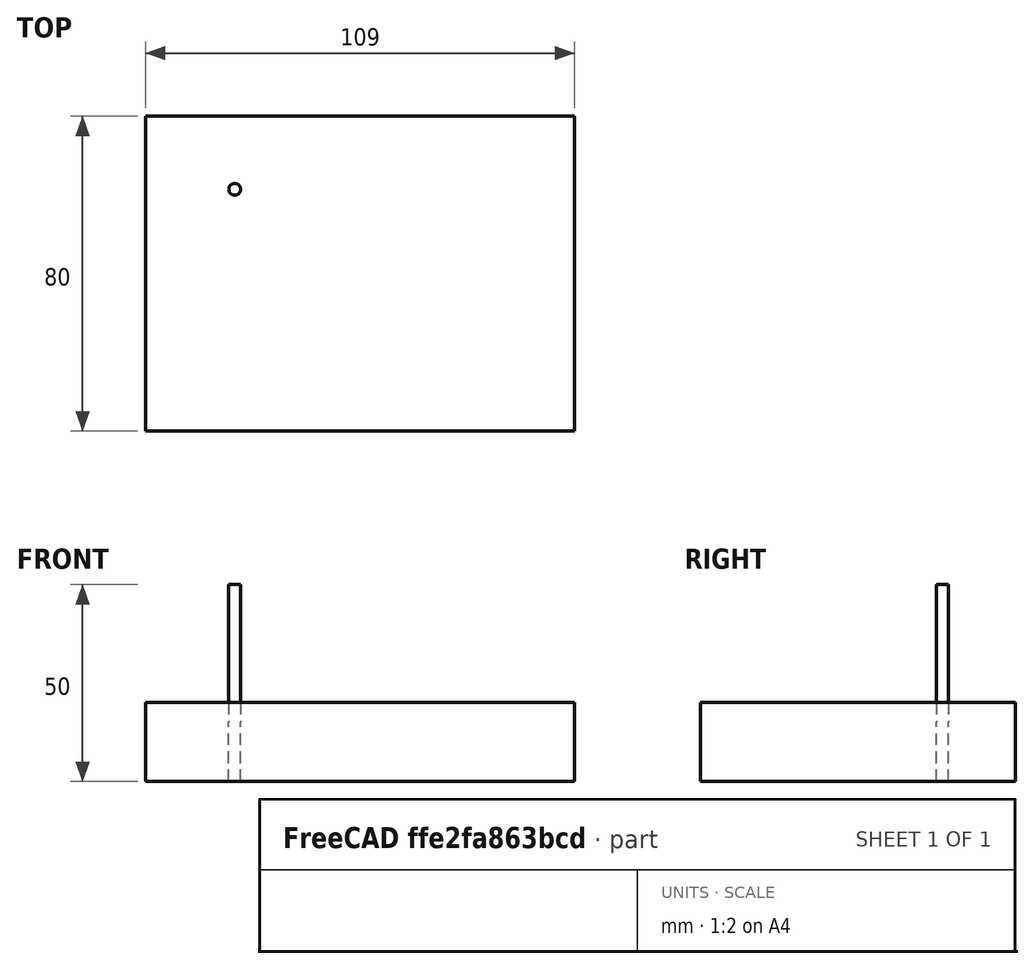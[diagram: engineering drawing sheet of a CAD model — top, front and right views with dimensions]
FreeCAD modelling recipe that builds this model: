
FCSTD DOCUMENT  (FreeCAD 0.21R33668 +26 (Git))
Label: Profile_20_80V_3mm
License: All rights reserved
LicenseURL: https://en.wikipedia.org/wiki/All_rights_reserved
objects: Path::FeaturePython×5, Sketcher::SketchObject×4, PartDesign::Pocket×3, Part::FeaturePython×3, App::DocumentObjectGroup×3, Mesh::FeaturePython×2, PartDesign::Pad×1, Spreadsheet::Sheet×1, App::FeaturePython×1, PartDesign::Fillet×1, PartDesign::Body×1
note: 21 computed .brp shape members not serialized (recipe doc carries the construction recipe); baked Part::Feature solids carry a one-line shape summary decoded from their .brp

FEATURE [Sketcher::SketchObject] Sketch  label="Sketch_Profile"
  FullyConstrained = true
  MapMode = 5
  Placement = pos=(0,0,0) rot=(1,0,0;1.5708rad)
  Support = -> [XZ_Plane]
  expr: Constraints[3] = Spreadsheet.Width
  expr: Constraints[4] = Spreadsheet.Height
  sketch-geometry (4):
    g0: LineSegment StartX=40 StartY=0 StartZ=0 EndX=40 EndY=-20 EndZ=0
    g1: LineSegment StartX=40 StartY=-20 StartZ=0 EndX=-40 EndY=-20 EndZ=0
    g2: LineSegment StartX=-40 StartY=-20 StartZ=0 EndX=-40 EndY=0 EndZ=0
    g3: LineSegment StartX=-40 StartY=0 StartZ=0 EndX=40 EndY=0 EndZ=0
  constraints (11):
    c: Horizontal(g1)
    c: Vertical(g0)
    c: Vertical(g2)
    c: DistanceX(g2,g0) = 80
    c: DistanceY(g2,g2) = 20
    c: Symmetric(g2,g0,g-1)
    c: Coincident(g3,g2)
    c: Horizontal(g3)
    c: Coincident(g0,g1)
    c: Coincident(g1,g2)
    c: Coincident(g3,g0)
FEATURE [PartDesign::Pad] Pad  label="Profile"
  Direction = (0,-1,-2e-16)
  Length = 105
  Length2 = 10
  Midplane = true
  Placement = pos=(0,0,0) rot=(1,0,0;1.5708rad)
  Profile = -> Sketch
  ReferenceAxis = -> Sketch [N_Axis]
  Type = 0
FEATURE [Spreadsheet::Sheet] Spreadsheet
  cells = A3='Height; B3(Height)=20; A4='Width; B4(Width)=80; A5='Slot_Height; B5(Slot_Height)=5.54; A7='V_Slot; B7(V_Slot)=20
FEATURE [App::FeaturePython] SetupSheet  # Path/CAM operation (typed FeaturePython)
  ClearanceHeightExpression = OpStockZMax+SetupSheet.ClearanceHeightOffset
  ClearanceHeightOffset = 15
  CoolantMode = 0
  CoolantModes = None | Flood | Mist
  FinalDepthExpression = OpFinalDepth
  HorizRapid = 6.66667
  SafeHeightExpression = OpStockZMax+SetupSheet.SafeHeightOffset
  SafeHeightOffset = 3
  StartDepthExpression = OpStartDepth
  StepDownExpression = OpToolDiameter
  VertRapid = 5
FEATURE [Sketcher::SketchObject] Sketch001
  ExternalGeometry = -> [Pad]
  FullyConstrained = true
  MapMode = 5
  Placement = pos=(0,0,0) rot=(0,0,1;3.14159rad)
  Support = -> [Pad]
  expr: Constraints[11] = 65
  expr: Constraints[12] = Spreadsheet.V_Slot
  expr: Constraints[8] = Spreadsheet.V_Slot
  expr: Constraints[9] = Spreadsheet.V_Slot
  sketch-geometry (8):
    g0: Circle CenterX=-30 CenterY=-42.5 CenterZ=0 NormalX=0 NormalY=0 NormalZ=1 AngleXU=0 Radius=2.75
    g1: Circle CenterX=30 CenterY=-42.5 CenterZ=0 NormalX=0 NormalY=0 NormalZ=1 AngleXU=0 Radius=2.75
    g2: Circle CenterX=-10 CenterY=42.5 CenterZ=0 NormalX=0 NormalY=0 NormalZ=1 AngleXU=0 Radius=2.75
    g3: Circle CenterX=10 CenterY=42.5 CenterZ=0 NormalX=0 NormalY=0 NormalZ=1 AngleXU=0 Radius=2.75
    g4: Circle CenterX=-10 CenterY=22.5 CenterZ=0 NormalX=0 NormalY=0 NormalZ=1 AngleXU=0 Radius=2.75
    g5: Circle CenterX=10 CenterY=22.5 CenterZ=0 NormalX=0 NormalY=0 NormalZ=1 AngleXU=0 Radius=2.75
    g6: Circle CenterX=-10 CenterY=-42.5 CenterZ=0 NormalX=0 NormalY=0 NormalZ=1 AngleXU=0 Radius=2.75
    g7: Circle CenterX=10 CenterY=-42.5 CenterZ=0 NormalX=0 NormalY=0 NormalZ=1 AngleXU=0 Radius=2.75
  constraints (24):
    c: Diameter(g0) = 5.5
    c: Equal(g0,g4)
    c: Equal(g4,g2)
    c: Equal(g2,g3)
    c: Equal(g3,g5)
    c: Horizontal(g4,g5)
    c: Vertical(g4,g2)
    c: Vertical(g5,g3)
    c: DistanceX(g4,g5) = 20
    c: DistanceY(g4,g2) = 20
    c: Horizontal(g2,g3)
    c: DistanceY(g0,g4) = 65
    c: DistanceX(g0,g4) = 20
    c: Horizontal(g1,g0)
    c: DistanceX(g-3,g0) = 10
    c: DistanceY(g-3,g0) = 10
    c: DistanceX(g0,g1) = 60
    c: Equal(g0,g1)
    c: Equal(g0,g6)
    c: Equal(g6,g7)
    c: Horizontal(g6,g7)
    c: Horizontal(g7,g0)
    c: Vertical(g6,g4)
    c: Vertical(g7,g5)
FEATURE [PartDesign::Pocket] Pocket
  BaseFeature = -> Pad
  Direction = (0,2e-16,-1)
  Length = 5
  Length2 = 5
  Placement = pos=(0,0,0) rot=(1,0,0;1.5708rad)
  Profile = -> Sketch001
  ReferenceAxis = -> Sketch001 [N_Axis]
  Type = 1
FEATURE [Part::FeaturePython] ToolBit  label="3mm Endmill"  # Path/CAM toolbit (typed FeaturePython)
  BitPropertyNames = Chipload | CuttingEdgeHeight | Diameter | Flutes | Length | Material | ShankDiameter | SpindleDirection
  BitShape = C:/Program Files/FreeCAD 0.21/Mod\Path\Tools\Shape\endmill.fcstd
  Chipload = 0
  CuttingEdgeHeight = 15
  Diameter = 3
  File = <userpath>/Desktop/CNC/ToolBit/Bit/3mm_Endmill.fctb
  Flutes = 0
  Length = 50
  Material = 0
  Placement = pos=(-86.3729,61.4237,-20) rot=(0,0,1;0rad)
  ShankDiameter = 3
  ShapeName = endmill
  SpindleDirection = 0
FEATURE [Path::FeaturePython] _mm_Endmill001  label="3mm Endmill001"  # Path/CAM operation (typed FeaturePython)
  HorizFeed = 7
  HorizRapid = 6.66667
  SpindleDir = 0
  SpindleSpeed = 8000
  Tool = -> ToolBit
  ToolNumber = 3
  VertFeed = 7
  VertRapid = 5
  expr: HorizRapid = SetupSheet.HorizRapid
  expr: VertRapid = SetupSheet.VertRapid
FEATURE [App::DocumentObjectGroup] Tools
  Group = -> [_mm_Endmill001]
FEATURE [Sketcher::SketchObject] Sketch002
  ExternalGeometry = -> [Pocket]
  FullyConstrained = true
  MapMode = 5
  Placement = pos=(0,0,0) rot=(0,0,1;3.14159rad)
  Support = -> [Pocket]
  sketch-geometry (8):
    g0: Circle CenterX=-10 CenterY=42.5 CenterZ=0 NormalX=0 NormalY=0 NormalZ=1 AngleXU=0 Radius=4.75
    g1: Circle CenterX=10 CenterY=42.5 CenterZ=0 NormalX=0 NormalY=0 NormalZ=1 AngleXU=0 Radius=4.75
    g2: Circle CenterX=-10 CenterY=22.5 CenterZ=0 NormalX=0 NormalY=0 NormalZ=1 AngleXU=0 Radius=4.75
    g3: Circle CenterX=10 CenterY=22.5 CenterZ=0 NormalX=0 NormalY=0 NormalZ=1 AngleXU=0 Radius=4.75
    g4: Circle CenterX=10 CenterY=-42.5 CenterZ=0 NormalX=0 NormalY=0 NormalZ=1 AngleXU=0 Radius=4.75
    g5: Circle CenterX=30 CenterY=-42.5 CenterZ=0 NormalX=0 NormalY=0 NormalZ=1 AngleXU=0 Radius=4.75
    g6: Circle CenterX=-30 CenterY=-42.5 CenterZ=0 NormalX=0 NormalY=0 NormalZ=1 AngleXU=0 Radius=4.75
    g7: Circle CenterX=-10 CenterY=-42.5 CenterZ=0 NormalX=0 NormalY=0 NormalZ=1 AngleXU=0 Radius=4.75
  constraints (16):
    c: Coincident(g0,g-3)
    c: Coincident(g1,g-4)
    c: Coincident(g2,g-5)
    c: Coincident(g3,g-6)
    c: Coincident(g4,g-7)
    c: Coincident(g5,g-8)
    c: Equal(g4,g2)
    c: Equal(g2,g0)
    c: Equal(g0,g1)
    c: Equal(g1,g3)
    c: Equal(g3,g5)
    c: Diameter(g4) = 9.5
    c: Coincident(g7,g-10)
    c: Coincident(g6,g-9)
    c: Equal(g4,g7)
    c: Equal(g7,g6)
FEATURE [PartDesign::Pocket] Pocket001
  AlongSketchNormal = false
  BaseFeature = -> Pocket
  Direction = (0,2e-16,-1)
  Length = 5.54
  Length2 = 5
  Placement = pos=(0,0,0) rot=(1,0,0;1.5708rad)
  Profile = -> Sketch002
  ReferenceAxis = -> Sketch002 [N_Axis]
  Type = 0
  expr: Length = Spreadsheet.Slot_Height
FEATURE [Sketcher::SketchObject] Sketch003
  ExternalGeometry = -> [Pocket001]
  FullyConstrained = true
  MapMode = 5
  Placement = pos=(0,0,0) rot=(0,0,1;3.14159rad)
  Support = -> [Pocket001]
  sketch-geometry (8):
    g0: LineSegment StartX=-40 StartY=52.5 StartZ=0 EndX=-19 EndY=52.5 EndZ=0
    g1: LineSegment StartX=-19 StartY=52.5 StartZ=0 EndX=-19 EndY=7.5 EndZ=0
    g2: LineSegment StartX=-19 StartY=7.5 StartZ=0 EndX=-40 EndY=7.5 EndZ=0
    g3: LineSegment StartX=-40 StartY=7.5 StartZ=0 EndX=-40 EndY=52.5 EndZ=0
    g4: LineSegment StartX=40 StartY=52.5 StartZ=0 EndX=19 EndY=52.5 EndZ=0
    g5: LineSegment StartX=19 StartY=52.5 StartZ=0 EndX=19 EndY=7.5 EndZ=0
    g6: LineSegment StartX=19 StartY=7.5 StartZ=0 EndX=40 EndY=7.5 EndZ=0
    g7: LineSegment StartX=40 StartY=7.5 StartZ=0 EndX=40 EndY=52.5 EndZ=0
  constraints (21):
    c: Coincident(g0,g1)
    c: Coincident(g1,g2)
    c: Coincident(g2,g3)
    c: Coincident(g3,g0)
    c: Horizontal(g2)
    c: Vertical(g1)
    c: Vertical(g3)
    c: Coincident(g0,g-3)
    c: Coincident(g4,g5)
    c: Coincident(g5,g6)
    c: Coincident(g6,g7)
    c: Coincident(g7,g4)
    c: Horizontal(g6)
    c: Vertical(g5)
    c: Vertical(g7)
    c: Coincident(g4,g-4)
    c: DistanceX(g0,g4) = 38
    c: DistanceY(g3,g3) = 45
    c: Equal(g3,g7)
    c: Symmetric(g0,g4,g-2)
    c: Horizontal(g0)
FEATURE [PartDesign::Pocket] Pocket002
  BaseFeature = -> Pocket001
  Direction = (0,2e-16,-1)
  Length = 5
  Length2 = 5
  Placement = pos=(0,0,0) rot=(1,0,0;1.5708rad)
  Profile = -> Sketch003
  ReferenceAxis = -> Sketch003 [N_Axis]
  Type = 1
FEATURE [PartDesign::Fillet] Fillet
  Base = -> Pocket002 [Edge3,Edge23,Edge40,Edge39,Edge38,Edge37]
  BaseFeature = -> Pocket002
  Placement = pos=(0,0,0) rot=(1,0,0;1.5708rad)
  Radius = 5
  SupportTransform = false
  UseAllEdges = false
FEATURE [PartDesign::Body] Body  label="Profile_with_Hole_5.5mm"
  Group = -> [Sketch,Pad,Sketch001,Pocket,Sketch002,Pocket001,Sketch003,Pocket002,Fillet]
  Origin = -> Origin
  Tip = -> Fillet
FEATURE [Part::FeaturePython] Clone  label="Model-Profile_with_Hole_5.5mm"  # Draft clone (typed FeaturePython)
  AttacherType = Attacher::AttachEngine3D
  Fuse = false
  Objects = -> [Body]
  PathResource = Model
  Placement = pos=(-52.5,40,-8.9e-15) rot=(0,0,-1;1.5708rad)
  Scale = (1,1,1)
FEATURE [App::DocumentObjectGroup] Model
  Group = -> [Clone]
FEATURE [Path::FeaturePython] Adaptive  label="Adaptive_OUTSIDE_CTBR"  # Path/CAM operation (typed FeaturePython)
  Active = true
  Base = -> [Clone]
  ClearanceHeight = 15
  CoolantMode = 0
  CycleTime = 00:05:41
  ExtensionCorners = true
  ExtensionLengthDefault = 1.5
  FinalDepth = -5.54
  FinishDepth = 0
  FinishingProfile = true
  ForceInsideOut = false
  HelixAngle = 5
  HelixConeAngle = 0
  HelixDiameterLimit = 0
  KeepToolDownRatio = 3
  LiftDistance = 0
  OpFinalDepth = -5.54
  OpStartDepth = 0
  OpStockZMax = 0
  OpStockZMin = -20
  OpToolDiameter = 3
  OperationType = 0
  SafeHeight = 3
  Side = 1
  StartDepth = 0
  StepDown = 6
  StepOver = 20
  StockToLeave = 0
  StopProcessing = false
  Stopped = false
  Tolerance = 0.1
  ToolController = -> _mm_Endmill001
  UseHelixArcs = false
  UseOutline = true
  expr: ClearanceHeight = OpStockZMax + SetupSheet.ClearanceHeightOffset
  expr: ExtensionLengthDefault = OpToolDiameter / 2
  expr: FinalDepth = OpFinalDepth
  expr: SafeHeight = OpStockZMax + SetupSheet.SafeHeightOffset
  expr: StartDepth = OpStartDepth
  expr: StepDown = OpToolDiameter * 2
FEATURE [Path::FeaturePython] Adaptive001  label="Adaptive_INSIDE_CTBR"  # Path/CAM operation (typed FeaturePython)
  Active = true
  Base = -> [Clone]
  ClearanceHeight = 15
  CoolantMode = 0
  CycleTime = 00:07:48
  ExtensionCorners = true
  ExtensionLengthDefault = 1.5
  FinalDepth = -15.46
  FinishDepth = 0
  FinishingProfile = true
  ForceInsideOut = false
  HelixAngle = 5
  HelixConeAngle = 0
  HelixDiameterLimit = 0
  KeepToolDownRatio = 3
  LiftDistance = 0
  OpFinalDepth = -20
  OpStartDepth = 0
  OpStockZMax = 0
  OpStockZMin = -20
  OpToolDiameter = 3
  OperationType = 0
  SafeHeight = 3
  Side = 1
  StartDepth = -5.54
  StepDown = 6
  StepOver = 20
  StockToLeave = 0
  StopProcessing = false
  Stopped = false
  Tolerance = 0.1
  ToolController = -> _mm_Endmill001
  UseHelixArcs = false
  UseOutline = true
  expr: ClearanceHeight = OpStockZMax + SetupSheet.ClearanceHeightOffset
  expr: ExtensionLengthDefault = OpToolDiameter / 2
  expr: FinalDepth = -Spreadsheet.Height + Spreadsheet.Slot_Height - 1
  expr: SafeHeight = OpStockZMax + SetupSheet.SafeHeightOffset
  expr: StartDepth = -Spreadsheet.Slot_Height
  expr: StepDown = OpToolDiameter * 2
FEATURE [Path::FeaturePython] Adaptive002  label="Adaptive_OUTSIDE_CUT"  # Path/CAM operation (typed FeaturePython)
  Active = true
  Base = -> [Clone]
  ClearanceHeight = 15
  CoolantMode = 0
  CycleTime = 00:16:16
  ExtensionCorners = true
  ExtensionLengthDefault = 1.5
  FinalDepth = -20
  FinishDepth = 0
  FinishingProfile = false
  ForceInsideOut = false
  HelixAngle = 5
  HelixConeAngle = 0
  HelixDiameterLimit = 1
  KeepToolDownRatio = 3
  LiftDistance = 0
  OpFinalDepth = -20
  OpStartDepth = 0
  OpStockZMax = 0
  OpStockZMin = -20
  OpToolDiameter = 3
  OperationType = 1
  SafeHeight = 3
  Side = 0
  StartDepth = 0
  StepDown = 6
  StepOver = 30
  StockToLeave = 0
  StopProcessing = false
  Stopped = false
  Tolerance = 0.1
  ToolController = -> _mm_Endmill001
  UseHelixArcs = false
  UseOutline = true
  expr: ClearanceHeight = OpStockZMax + SetupSheet.ClearanceHeightOffset
  expr: ExtensionLengthDefault = OpToolDiameter / 2
  expr: SafeHeight = OpStockZMax + SetupSheet.SafeHeightOffset
  expr: StepDown = OpToolDiameter * 2
FEATURE [App::DocumentObjectGroup] Operations
  Group = -> [Adaptive,Adaptive001,Adaptive002]
FEATURE [Part::FeaturePython] Stock  # WARN: FeaturePython — macro-defined, semantics opaque (R4)
  Base = -> Model
  ExtXneg = 4
  ExtXpos = 0
  ExtYneg = 0
  ExtYpos = 0
  ExtZneg = 0
  ExtZpos = 0
  Placement = pos=(-105,-2.84e-14,-20) rot=(0,0,1;0rad)
  StockType = FromBase
FEATURE [Path::FeaturePython] Job  # Path/CAM operation (typed FeaturePython)
  CycleTime = 00:29:45
  Fixtures = G54
  GeometryTolerance = 0.01
  JobType = 0
  LastPostProcessDate = 2024-02-14 00:18:21.522914
  LastPostProcessOutput = <userpath>\Desktop\CNC\FC_CNC_Template\Profile_20_80V_3mm.nc
  Model = -> Model
  Operations = -> Operations
  OrderOutputBy = 2
  PostProcessor = 10
  PostProcessorArgs = --bcnc --no-translate_drill
  PostProcessorOutputFile = <userpath>/Desktop/CNC/FC_CNC_Template/Profile_20_80V_3mm.nc
  SetupSheet = -> SetupSheet
  SplitOutput = false
  Stock = -> Stock
  Tools = -> Tools
FEATURE [Mesh::FeaturePython] CutMaterial  # WARN: FeaturePython — macro-defined, semantics opaque (R4)
FEATURE [Mesh::FeaturePython] CutMaterial001  # WARN: FeaturePython — macro-defined, semantics opaque (R4)
